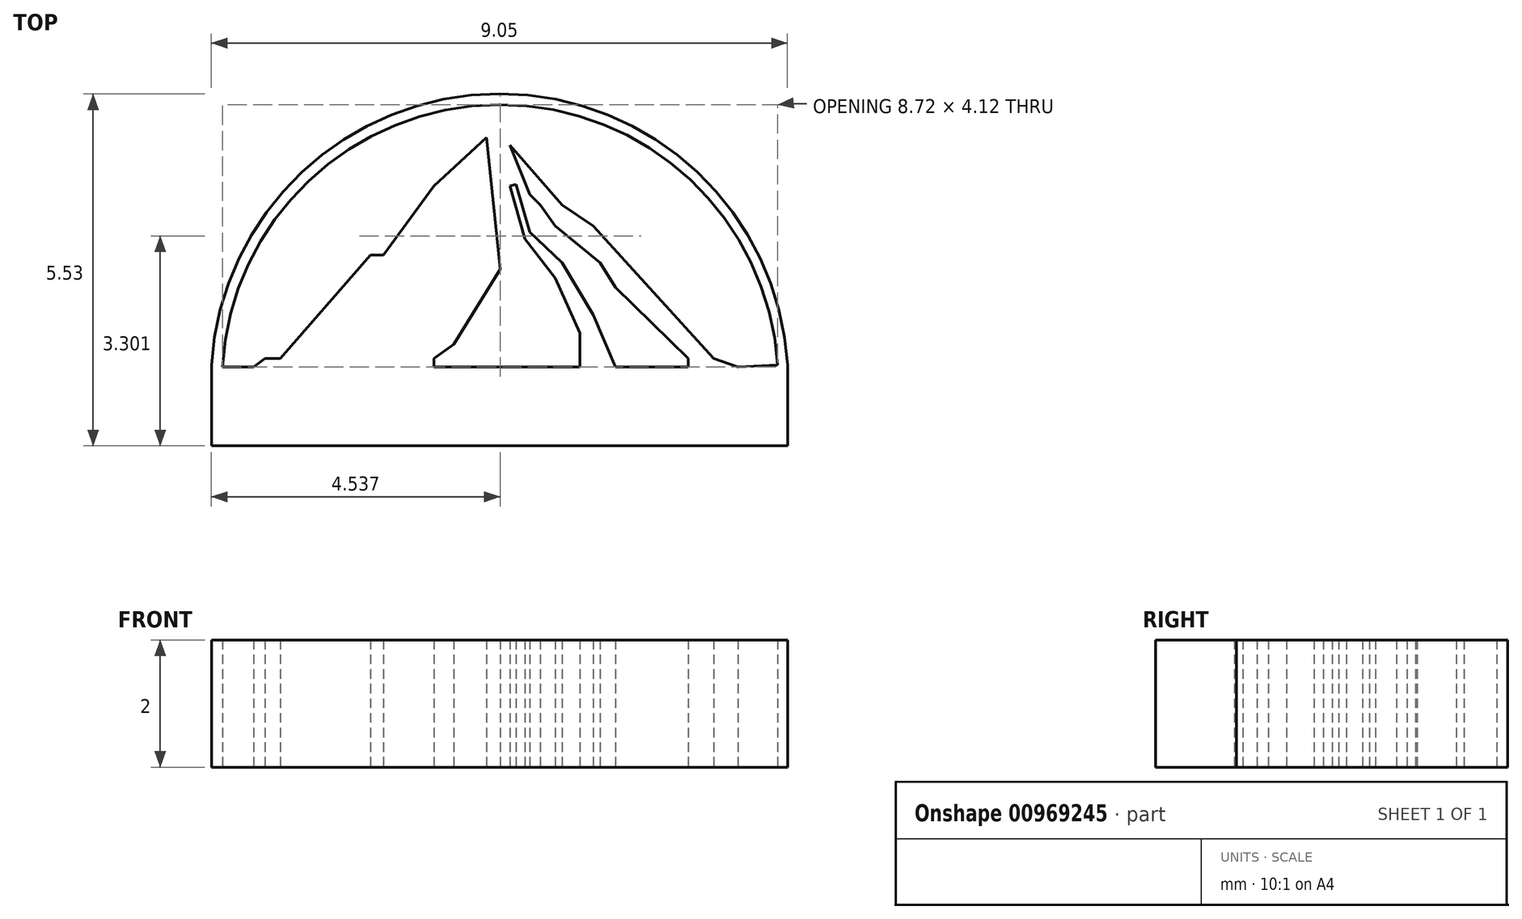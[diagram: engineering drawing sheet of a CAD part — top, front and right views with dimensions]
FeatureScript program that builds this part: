
annotation { "Feature Type Name" : "Feature", "Feature Type Description" : "" }
export const myFeature = defineFeature(function(context is Context, id is Id, definition is map)
    precondition{}
    {
        {
            var Q0;
            Q0=qCreatedBy(makeId("Top.planeOp"),FACE);
            var sketch = newSketch(context, id + "F0", { "sketchPlane" : qUnion([Q0])});
            skArc(sketch, "E0", {"start": v(4.58, -3.12) * mm, "mid": v(0.2, 0.97) * mm, "end": v(-4.14, -3.15) * mm});
            skArc(sketch, "E1", {"start": v(4.73, -3.12) * mm, "mid": v(0.2, 1.14) * mm, "end": v(-4.32, -3.12) * mm});
            skLineSegment(sketch, "E2", {"start": v(-4.14, -3.15) * mm, "end": v(-3.65, -3.15) * mm});
            skLineSegment(sketch, "E3", {"start": v(-3.65, -3.15) * mm, "end": v(-3.48, -3.01) * mm});
            skLineSegment(sketch, "E4", {"start": v(-3.48, -3.01) * mm, "end": v(-3.23, -3.01) * mm});
            skLineSegment(sketch, "E5", {"start": v(-3.23, -3.01) * mm, "end": v(-1.82, -1.39) * mm});
            skLineSegment(sketch, "E6", {"start": v(-1.82, -1.39) * mm, "end": v(-1.62, -1.39) * mm});
            skLineSegment(sketch, "E7", {"start": v(-1.62, -1.39) * mm, "end": v(-0.82, -0.3) * mm});
            skLineSegment(sketch, "E8", {"start": v(-0.82, -0.3) * mm, "end": v(0, 0.46) * mm});
            skLineSegment(sketch, "E9", {"start": v(0, 0.46) * mm, "end": v(0.22, -1.61) * mm});
            skLineSegment(sketch, "E10", {"start": v(0.22, -1.61) * mm, "end": v(-0.51, -2.8) * mm});
            skLineSegment(sketch, "E11", {"start": v(-0.51, -2.8) * mm, "end": v(-0.82, -3.01) * mm});
            skLineSegment(sketch, "E12", {"start": v(-0.82, -3.01) * mm, "end": v(-0.82, -3.15) * mm});
            skLineSegment(sketch, "E13", {"start": v(-0.82, -3.15) * mm, "end": v(1.47, -3.15) * mm});
            skLineSegment(sketch, "E14", {"start": v(1.47, -3.15) * mm, "end": v(1.47, -2.62) * mm});
            skLineSegment(sketch, "E15", {"start": v(1.47, -2.62) * mm, "end": v(1.08, -1.75) * mm});
            skLineSegment(sketch, "E16", {"start": v(1.08, -1.75) * mm, "end": v(0.6, -1.13) * mm});
            skLineSegment(sketch, "E17", {"start": v(0.6, -1.13) * mm, "end": v(0.37, -0.3) * mm});
            skLineSegment(sketch, "E18", {"start": v(0.37, -0.3) * mm, "end": v(0.47, -0.28) * mm});
            skLineSegment(sketch, "E19", {"start": v(0.47, -0.28) * mm, "end": v(0.6, -0.76) * mm});
            skLineSegment(sketch, "E20", {"start": v(0.6, -0.76) * mm, "end": v(0.68, -1.03) * mm});
            skLineSegment(sketch, "E21", {"start": v(0.68, -1.03) * mm, "end": v(1.2, -1.51) * mm});
            skLineSegment(sketch, "E22", {"start": v(1.2, -1.51) * mm, "end": v(1.68, -2.33) * mm});
            skLineSegment(sketch, "E23", {"start": v(1.68, -2.33) * mm, "end": v(2.03, -3.15) * mm});
            skLineSegment(sketch, "E24", {"start": v(2.03, -3.15) * mm, "end": v(3.17, -3.15) * mm});
            skLineSegment(sketch, "E25", {"start": v(3.17, -3.15) * mm, "end": v(3.17, -3.01) * mm});
            skLineSegment(sketch, "E26", {"start": v(3.17, -3.01) * mm, "end": v(2.03, -1.9) * mm});
            skLineSegment(sketch, "E27", {"start": v(2.03, -1.9) * mm, "end": v(1.79, -1.51) * mm});
            skLineSegment(sketch, "E28", {"start": v(1.79, -1.51) * mm, "end": v(1.08, -0.94) * mm});
            skLineSegment(sketch, "E29", {"start": v(1.08, -0.94) * mm, "end": v(0.85, -0.6) * mm});
            skLineSegment(sketch, "E30", {"start": v(0.85, -0.6) * mm, "end": v(0.68, -0.44) * mm});
            skLineSegment(sketch, "E31", {"start": v(0.68, -0.44) * mm, "end": v(0.37, 0.34) * mm});
            skLineSegment(sketch, "E32", {"start": v(0.37, 0.34) * mm, "end": v(1.2, -0.6) * mm});
            skLineSegment(sketch, "E33", {"start": v(1.2, -0.6) * mm, "end": v(1.68, -0.94) * mm});
            skLineSegment(sketch, "E34", {"start": v(1.68, -0.94) * mm, "end": v(3.57, -3.01) * mm});
            skLineSegment(sketch, "E35", {"start": v(3.57, -3.01) * mm, "end": v(3.96, -3.15) * mm});
            skLineSegment(sketch, "E36", {"start": v(3.96, -3.15) * mm, "end": v(4.58, -3.12) * mm});
            skLineSegment(sketch, "E37", {"start": v(-4.32, -3.12) * mm, "end": v(-4.32, -4.39) * mm});
            skLineSegment(sketch, "E38", {"start": v(-4.32, -4.39) * mm, "end": v(4.73, -4.39) * mm});
            skLineSegment(sketch, "E39", {"start": v(4.73, -4.39) * mm, "end": v(4.73, -3.12) * mm});
            skSolve(sketch);
        }
        {
            var Q0;
            Q0 = qSketchRegion(id + "F0", true);
            extrude(context, id + "F1", {"entities" : qUnion([Q0]), "depth" : 2 * mm, "offsetDistance" : 25 * mm});
        }
    });
